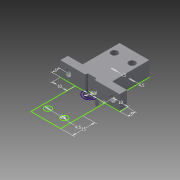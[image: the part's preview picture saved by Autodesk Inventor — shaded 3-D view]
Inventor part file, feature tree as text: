
AUTODESK INVENTOR PART (.ipt)
format: ipt  version: 2015 (Build 190159000, 159)  size: 134,656 bytes
history: native  units: in
note: dims shown in document units (in); Inventor stores cm internally (conversion verified against a paired STEP export)
features: extrude x4, sketch x2
ambient origin geometry x8: Origin, YZ Plane, XZ Plane, XY Plane, X Axis, Y Axis, Z Axis, Center Point
bodies: Body1 (feature_tree)
feature tree (6):
  sketch  "Sketch1"  dims[d0=0.248in d6=0.5906in]
  extrude  "Extrusion10"  Depth=0.5906in
  extrude  "Extrusion11"  Depth=0.3937in
  extrude  "Extrusion12"  Depth=0.1969in
  extrude  "Extrusion13"  Depth=0.3937in
  sketch  "Sketch3"  dims[d34=0.3543in d35=0.3937in d36=0.1969in d37=0.3937in d38=0.1969in d43=0.1772in d44=0.1772in d45=0.1772in d46=0.1772in d47=0.3937in d48=0.0in d49=0.1969in d50=0.0in d51=0.1969in d52=0.1969in d53=0.1969in d54=0.1969in d55=0.1772in d56=0.1772in d57=0.3937in d58=0.0in d59=0.0157in d60=0.3937in d61=0.0in]
